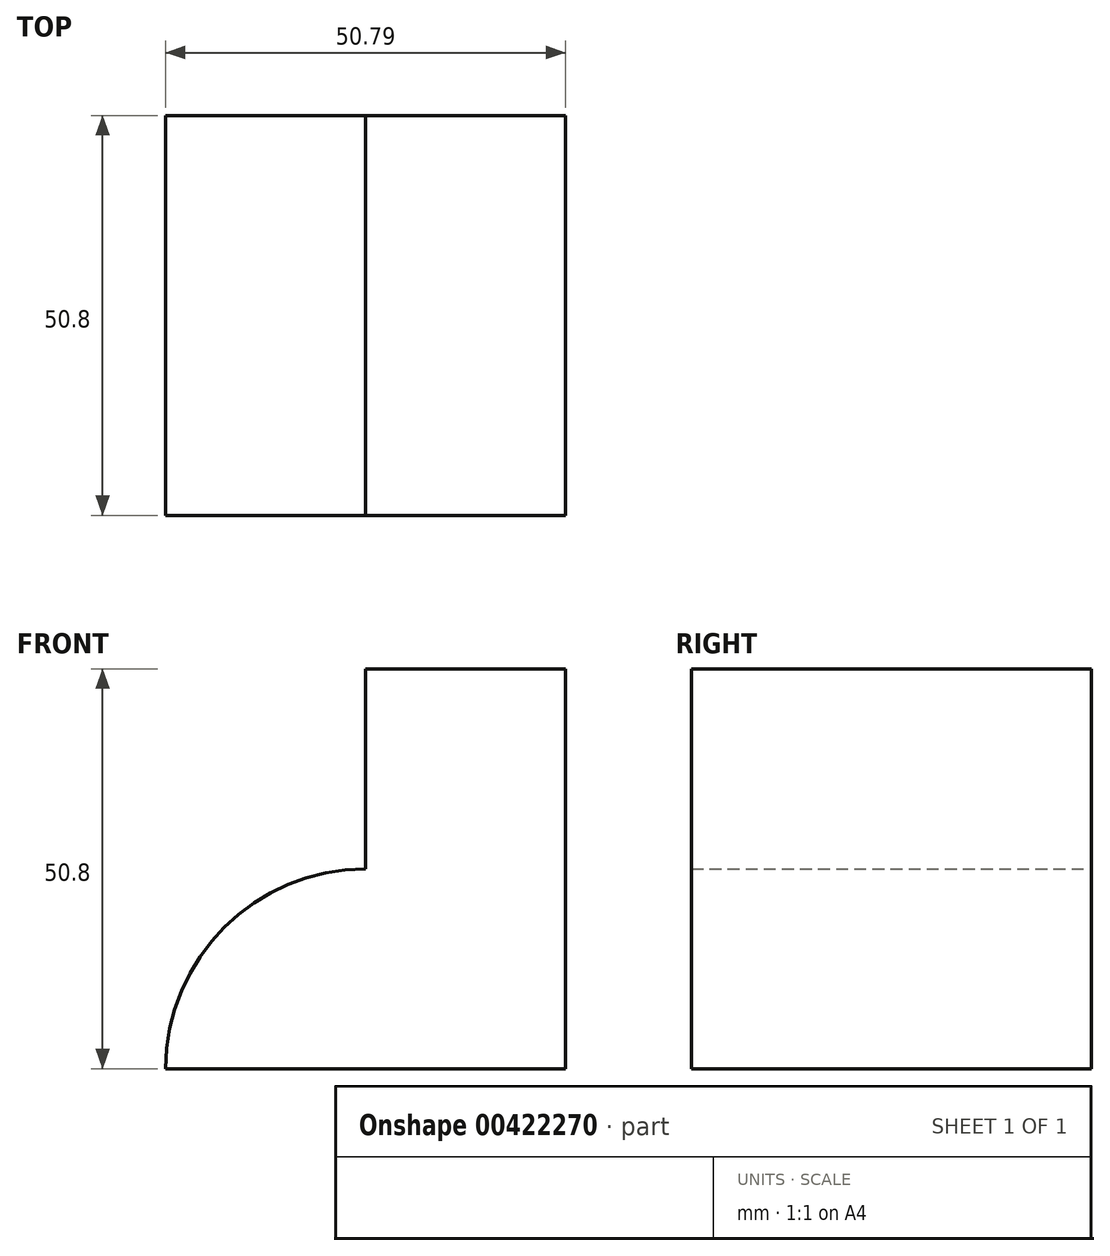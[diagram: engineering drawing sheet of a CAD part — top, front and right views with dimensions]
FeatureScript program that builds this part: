
annotation { "Feature Type Name" : "Feature", "Feature Type Description" : "" }
export const myFeature = defineFeature(function(context is Context, id is Id, definition is map)
    precondition{}
    {
        {
            var Q0;
            Q0=qCreatedBy(makeId("Front.planeOp"),FACE);
            var sketch = newSketch(context, id + "F0", { "sketchPlane" : qUnion([Q0])});
            skLineSegment(sketch, "E0", {"start": v(-14.13, -43.35) * mm, "end": v(36.66, -43.35) * mm});
            skLineSegment(sketch, "E1", {"start": v(36.66, -43.35) * mm, "end": v(36.66, 7.45) * mm});
            skLineSegment(sketch, "E2", {"start": v(36.66, 7.45) * mm, "end": v(11.27, 7.45) * mm});
            skLineSegment(sketch, "E3", {"start": v(11.27, 7.45) * mm, "end": v(11.27, -17.95) * mm});
            skArc(sketch, "E4", {"start": v(11.27, -17.95) * mm, "mid": v(-6.67, -25.4) * mm, "end": v(-14.13, -43.35) * mm});
            skSolve(sketch);
        }
        {
            var Q0;
            Q0=makeQuery(id+"F0.imprint","IMPRINT",FACE,{"disambiguationData":[TD([[makeQuery(id+"F0.imprint","IMPRINT",EDGE,{"derivedFrom":sQuery(id+"F0.wireOp",EDGE,"E0")}),1.0]])]});
            extrude(context, id + "F1", {"entities" : qUnion([Q0]), "depth" : 50.8 * mm});
        }
    });
